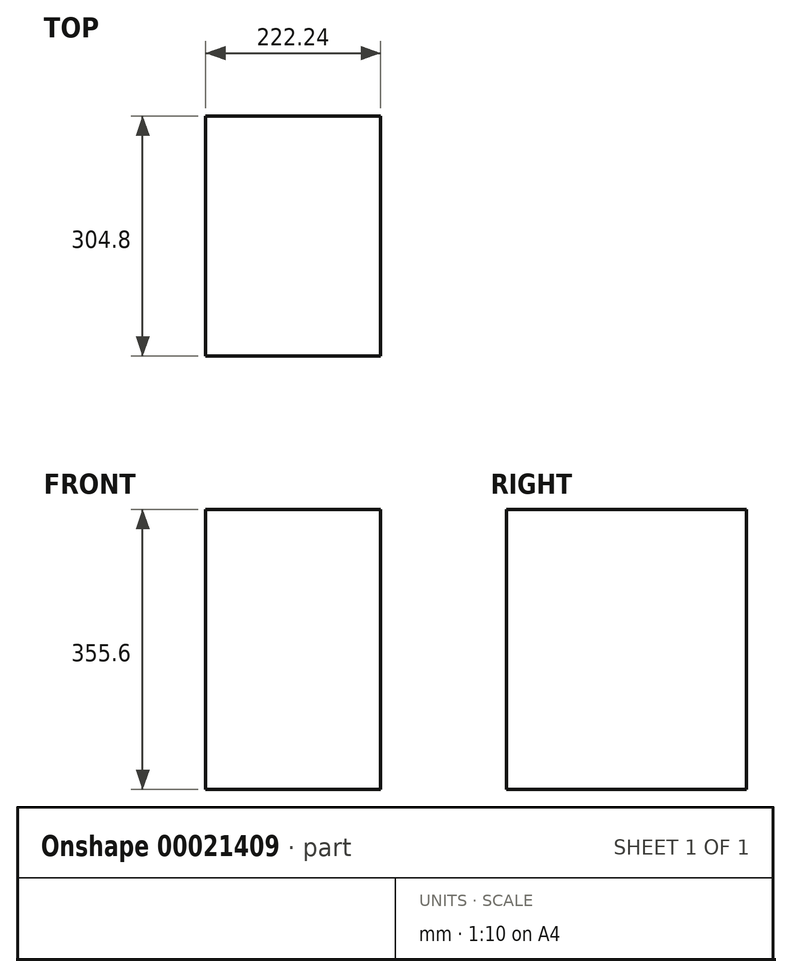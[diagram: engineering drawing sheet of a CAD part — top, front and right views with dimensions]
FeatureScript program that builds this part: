
annotation { "Feature Type Name" : "Feature", "Feature Type Description" : "" }
export const myFeature = defineFeature(function(context is Context, id is Id, definition is map)
    precondition{}
    {
        {
            var Q0;
            Q0=qCreatedBy(makeId("Front.planeOp"),FACE);
            var sketch = newSketch(context, id + "F0", { "sketchPlane" : qUnion([Q0])});
            skLineSegment(sketch, "E0.rect.bottom", {"start": v(111.13, 177.8) * mm, "end": v(-111.12, 177.8) * mm});
            skLineSegment(sketch, "E0.rect.top", {"start": v(111.12, -177.8) * mm, "end": v(-111.12, -177.8) * mm});
            skLineSegment(sketch, "E0.rect.left", {"start": v(111.13, 177.8) * mm, "end": v(111.13, -177.8) * mm});
            skLineSegment(sketch, "E0.rect.right", {"start": v(-111.12, 177.8) * mm, "end": v(-111.13, -177.8) * mm});
            skPoint(sketch, "E0.rect.middle", {"position": v(0, 0) * mm});
            skSolve(sketch);
        }
        {
            var Q0;
            Q0=makeQuery(id+"F0.imprint","IMPRINT",FACE,{"disambiguationData":[TD([[makeQuery(id+"F0.imprint","IMPRINT",EDGE,{"derivedFrom":sQuery(id+"F0.wireOp",EDGE,"E0.rect.bottom")}),1.0]])]});
            extrude(context, id + "F1", {"entities" : qUnion([Q0]), "depth" : 304.8 * mm});
        }
    });
